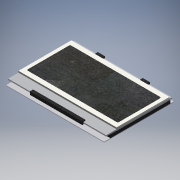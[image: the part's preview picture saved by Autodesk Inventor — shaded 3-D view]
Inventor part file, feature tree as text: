
AUTODESK INVENTOR PART (.ipt)
format: ipt  version: 2017 (Build 210142000, 142)  size: 271,360 bytes
history: native  units: mm
features: extrude x8, sketch x8, projected_geometry x5
ambient origin geometry x8: Origin, YZ Plane, XZ Plane, XY Plane, X Axis, Y Axis, Z Axis, Center Point
bodies: Volumenkörper1 (feature_tree), Volumenkörper3 (feature_tree), Volumenkörper4 (feature_tree), Volumenkörper5 (feature_tree), Volumenkörper6 (feature_tree), Volumenkörper7 (feature_tree), Volumenkörper8 (feature_tree), Volumenkörper9 (feature_tree)
feature tree (21):
  extrude  "LED_Platine"  Depth=67.0mm
  extrude  "LED_Rand"  Depth=3.5mm
  extrude  "LED_Beleuchtung"  Depth=1.3mm
  extrude  "LCD_Back"  Depth=1.3mm
  extrude  "LCD_BackGlas"  Depth=3.0mm TaperAngle=0.0deg
  extrude  "LCD_FrontGlas"  Depth=1.3mm
  extrude  "LCD_AA"  Depth=1.95mm
  extrude  "Extrusion9"  Depth=1.15mm TaperAngle=0.0deg
  sketch  "Skizze1"  dims[d0=94.1mm d1=67.0mm]
  sketch  "Skizze2"  dims[d2=0.55mm d3=0.0mm d4=3.5mm]
  sketch  "Skizze3"  dims[d5=6.0mm d8=1.3mm]
  projected_geometry  "Projizierte Kontur1"
  sketch  "Skizze4"  dims[d9=1.3mm d10=1.3mm]
  sketch  "Skizze5"  dims[d11=7.0mm d12=3.0mm d13=0.0mm]
  projected_geometry  "Projizierte Kontur2"
  sketch  "Skizze6"  dims[d14=3.0mm d15=0.0mm d16=1.3mm]
  projected_geometry  "Projizierte Kontur3"
  sketch  "Skizze7"  dims[d17=0.3mm d18=0.0mm d19=1.95mm]
  projected_geometry  "Projizierte Kontur4"
  sketch  "Skizze8"  dims[d20=1.95mm d21=1.15mm d22=0.0mm d23=2.4mm d24=10.0mm d25=1.5mm d26=0.0mm d27=0.1mm d28=0.0mm d29=3.35mm d30=4.55mm d31=3.35mm d32=4.55mm d33=1.0mm d34=22.0mm d35=7.0mm d36=1.0mm d37=7.0mm d38=2.0mm d39=22.0mm d40=7.0mm d41=1.0mm d42=7.0mm d43=2.0mm d44=22.0mm d45=22.0mm d46=1.0mm d47=2.0mm d48=1.0mm d49=2.0mm d50=0.0mm d51=0.0mm]
  projected_geometry  "Projizierte Kontur5"
